# Revit family: VE_Ventilation Unit_F_MEPcontent_ClimaRad_Ventura V1C_NL-NL
name_source: partatom
category: Mechanical Equipment
units: mm (PartAtom-declared; Revit-internal decimal feet)

## family parameters
Cut with Voids When Loaded = No
Host = Face
OmniClass Number = 23.75.70.21.24
OmniClass Title = Air Terminal Units
Part Type = Normal
Room Calculation Point = Yes
Round Connector Dimension = Use Diameter
Shared = No

## types (1)
- Ventura V1C
    Article Description = Ventileren, verwarmen en koelen
    Article Type = Ventura V1C
    Base Family Version = 12.19
    Content Supplier URL = www.MEPcontent.com
    Custom = No
    Default Elevation = 0 mm  [stored 0 ft]
    Depth = 200 mm  [stored 0.656168 ft]
    Description = Ventileren, verwarmen en koelen
    Double Rectangular Black = Grille Type : Brick-sized 104x205 Black
    Double Rectangular Brown = Grille Type : Brick-sized 104x205 Brown
    Double Rectangular White = Grille Type : Brick-sized 104x205 White
    EMCS Version = 4.0
    ETIM Article Class = EC010004
    Family Version = 11.26
    GLN = 8719279000001
    Grey = Color RGB 100-100-100
    Height = 2285 mm  [stored 7.49672 ft]
    Horizontal Left = Position : Horizontal, Left Corner
    Horizontal Right = Position : Horizontal, Right Corner
    IFCExportAs = IfcAirTerminal
    IFCExportType = NOTDEFINED
    MEPcontent Class = VENTILATION_UNIT
    Manufacturer = ClimaRad
    Manufacturer Art. No. = 3540300
    Manufacturer URL = https://www.climarad.nl
    Model = Ventura V1C
    Product Line = ClimaRad
    Rectangular Black = Grille Type : Brick-sized 53x210 Black
    Rectangular Brown = Grille Type : Brick-sized 53x210 Brown
    Rectangular White = Grille Type : Brick-sized 53x210 White
    Revit Version = 2018
    Square Grey = Grille Type : Surface-mounted 127x127 Grey
    Square White = Grille Type : Surface-mounted 127x127 White
    URL = https://mep.trimble.com
    Vertical Left = Position : Vertical, Left Corner
    Vertical Right = Position : Vertical, Right Corner
    Voltage = 230 V
    White = Color RAL 9016
    Width = 520 mm  [stored 1.70604 ft]

note: [stored X ft] marks values corroborated as IEEE doubles in the binary element streams (Revit-internal decimal feet)

## geometry (parser evidence)
native form markers: Sweep x13
no freeform markers — native parametric forms only
